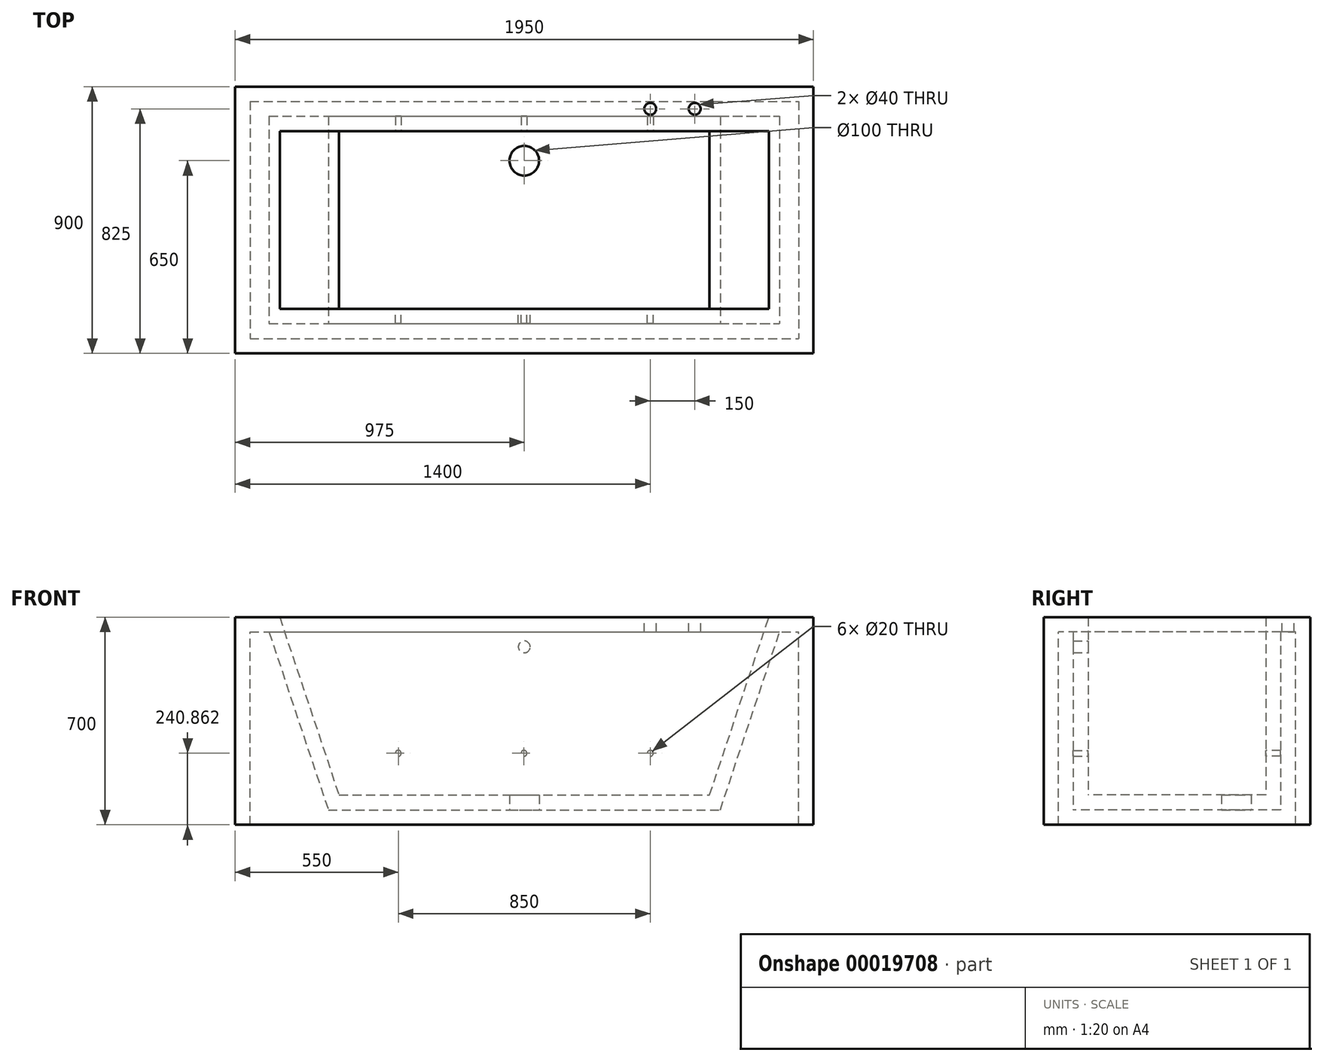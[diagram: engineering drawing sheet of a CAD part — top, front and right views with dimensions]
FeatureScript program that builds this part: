
annotation { "Feature Type Name" : "Feature", "Feature Type Description" : "" }
export const myFeature = defineFeature(function(context is Context, id is Id, definition is map)
    precondition{}
    {
        {
            var Q0;
            Q0=qCreatedBy(makeId("Front.planeOp"),FACE);
            var sketch = newSketch(context, id + "F0", { "sketchPlane" : qUnion([Q0])});
            skLineSegment(sketch, "E0.bottom", {"start": v(0, 0) * mm, "end": v(1950, 0) * mm});
            skLineSegment(sketch, "E0.top", {"start": v(0, 700) * mm, "end": v(1950, 700) * mm});
            skLineSegment(sketch, "E0.left", {"start": v(0, 0) * mm, "end": v(0, 700) * mm});
            skLineSegment(sketch, "E0.right", {"start": v(1950, 0) * mm, "end": v(1950, 700) * mm});
            skSolve(sketch);
        }
        {
            var Q0;
            Q0=makeQuery(id+"F0.imprint","IMPRINT",FACE,{"disambiguationData":[TD([[makeQuery(id+"F0.imprint","IMPRINT",EDGE,{"derivedFrom":sQuery(id+"F0.wireOp",EDGE,"E0.bottom")}),1.0]])]});
            var sketch = newSketch(context, id + "F1", { "sketchPlane" : qUnion([Q0])});
            skLineSegment(sketch, "E1", {"start": v(150, 700) * mm, "end": v(1800, 700) * mm});
            skLineSegment(sketch, "E2", {"start": v(150, 700) * mm, "end": v(350, 100) * mm});
            skLineSegment(sketch, "E3", {"start": v(350, 100) * mm, "end": v(1600, 100) * mm});
            skLineSegment(sketch, "E4", {"start": v(1600, 100) * mm, "end": v(1800, 700) * mm});
            skSolve(sketch);
        }
        {
            var Q0;
            Q0=makeQuery(id+"F0.imprint","IMPRINT",FACE,{"disambiguationData":[TD([[makeQuery(id+"F0.imprint","IMPRINT",EDGE,{"derivedFrom":sQuery(id+"F0.wireOp",EDGE,"E0.bottom")}),1.0]])]});
            extrude(context, id + "F2", {"entities" : qUnion([Q0]), "oppositeDirection" : true, "depth" : 450 * mm});
        }
        {
            var Q0;
            Q0=makeQuery(id+"F1.imprint","IMPRINT",FACE,{"disambiguationData":[TD([[makeQuery(id+"F1.imprint","IMPRINT",EDGE,{"derivedFrom":sQuery(id+"F1.wireOp",EDGE,"E1")}),-1.0]])]});
            extrude(context, id + "F3", {"entities" : qUnion([Q0]), "operationType" : NewBodyOperationType.REMOVE, "oppositeDirection" : true, "depth" : 300 * mm});
        }
        {
            var Q0;
            {var subQ0=makeQuery(id+"F2.opExtrude","SWEPT_FACE",FACE,{"disambiguationData":[OSD([sQuery(id+"F0.wireOp",EDGE,"E0.bottom")])]});Q0=makeQuery(id+"F7.boolean.opBoolean","MERGE",FACE,{"derivedFrom":[subQ0,makeQuery(id+"F7.opPattern","COPY",FACE,{"derivedFrom":subQ0,"instanceName":"1"})]});}
            var Q1;
            Q1=makeQuery(id+"F2.opExtrude","CAP_FACE",FACE,{"disambiguationData":[OSD([sQuery(id+"F0.wireOp",EDGE,"E0.bottom"),sQuery(id+"F0.wireOp",EDGE,"E0.top"),sQuery(id+"F0.wireOp",EDGE,"E0.left"),sQuery(id+"F0.wireOp",EDGE,"E0.right")])],"isStart":true});
            shell(context, id + "F4", {"entities" : qUnion([Q0, Q1]), "thickness" : 50 * mm});
        }
        {
            var Q0;
            Q0=makeQuery(id+"F3.boolean.opBoolean","COPY",FACE,{"derivedFrom":makeQuery(id+"F3.opExtrude","CAP_FACE",FACE,{"disambiguationData":[OSD([sQuery(id+"F1.wireOp",EDGE,"E1"),sQuery(id+"F1.wireOp",EDGE,"E2"),sQuery(id+"F1.wireOp",EDGE,"E3"),sQuery(id+"F1.wireOp",EDGE,"E4")])],"isStart":false})});
            var sketch = newSketch(context, id + "F5", { "sketchPlane" : qUnion([Q0])});
            skLineSegment(sketch, "E5", {"start": v(1600, 240.86) * mm, "end": v(1600, 100) * mm, "construction": true});
            skLineSegment(sketch, "E6", {"start": v(350, 240.86) * mm, "end": v(350, 100) * mm, "construction": true});
            skPoint(sketch, "E7", {"position": v(975, 240.86) * mm});
            skPoint(sketch, "E8", {"position": v(550, 240.86) * mm});
            skPoint(sketch, "E9", {"position": v(1400, 240.86) * mm});
            skLineSegment(sketch, "E10", {"start": v(350, 240.86) * mm, "end": v(550, 240.86) * mm, "construction": true});
            skLineSegment(sketch, "E11", {"start": v(1400, 240.86) * mm, "end": v(1600, 240.86) * mm, "construction": true});
            skLineSegment(sketch, "E12", {"start": v(550, 240.86) * mm, "end": v(1400, 240.86) * mm, "construction": true});
            skCircle(sketch, "E13", {"center": v(550, 240.86) * mm, "radius": 10 * mm});
            skCircle(sketch, "E14", {"center": v(974.1, 240.86) * mm, "radius": 10 * mm});
            skCircle(sketch, "E15", {"center": v(1400, 240.86) * mm, "radius": 10 * mm});
            skSolve(sketch);
        }
        {
            var Q0;
            Q0 = qSketchRegion(id + "F5", true);
            extrude(context, id + "F6", {"entities" : qUnion([Q0]), "operationType" : NewBodyOperationType.REMOVE, "oppositeDirection" : true, "depth" : 60 * mm});
        }
        {
            var Q0;
            Q0=makeQuery(id+"F2.opExtrude","SWEPT_BODY",BODY,{"disambiguationData":[OSD([sQuery(id+"F0.wireOp",EDGE,"E0.bottom"),sQuery(id+"F0.wireOp",EDGE,"E0.top"),sQuery(id+"F0.wireOp",EDGE,"E0.left"),sQuery(id+"F0.wireOp",EDGE,"E0.right")])]});
            var Q1;
            Q1=makeQuery(id+"F2.opExtrude","CAP_FACE",FACE,{"disambiguationData":[OSD([sQuery(id+"F0.wireOp",EDGE,"E0.bottom"),sQuery(id+"F0.wireOp",EDGE,"E0.top"),sQuery(id+"F0.wireOp",EDGE,"E0.left"),sQuery(id+"F0.wireOp",EDGE,"E0.right")])],"isStart":true});
            mirror(context, id + "F7", {"operationType" : NewBodyOperationType.ADD, "entities" : qUnion([Q0]), "mirrorPlane" : qUnion([Q1])});
        }
        {
            var Q0;
            {var subQ0=makeQuery(id+"F2.opExtrude","SWEPT_FACE",FACE,{"disambiguationData":[OSD([sQuery(id+"F0.wireOp",EDGE,"E0.top")])]});Q0=makeQuery(id+"F7.boolean.opBoolean","MERGE",FACE,{"derivedFrom":[subQ0,makeQuery(id+"F7.opPattern","COPY",FACE,{"derivedFrom":subQ0,"instanceName":"1"})]});}
            var sketch = newSketch(context, id + "F8", { "sketchPlane" : qUnion([Q0])});
            skLineSegment(sketch, "E16", {"start": v(1550, 450) * mm, "end": v(1550, 300) * mm, "construction": true});
            skLineSegment(sketch, "E17", {"start": v(1400, 450) * mm, "end": v(1400, 300) * mm, "construction": true});
            skLineSegment(sketch, "E18", {"start": v(0, 375) * mm, "end": v(1950, 375) * mm, "construction": true});
            skPoint(sketch, "E19", {"position": v(1400, 375) * mm});
            skPoint(sketch, "E20", {"position": v(1550, 375) * mm});
            skSolve(sketch);
        }
        {
            var Q0;
            Q0=sQuery(id+"F8.wireOp",VERTEX,"E20");
            var Q1;
            Q1=makeQuery(id+"F2.opExtrude","SWEPT_BODY",BODY,{"disambiguationData":[OSD([sQuery(id+"F0.wireOp",EDGE,"E0.bottom"),sQuery(id+"F0.wireOp",EDGE,"E0.top"),sQuery(id+"F0.wireOp",EDGE,"E0.left"),sQuery(id+"F0.wireOp",EDGE,"E0.right")])]});
            hole(context, id + "F9", {"style" : HoleStyle.SIMPLE, "holeDiameter" : 40 * mm, "endStyle" : HoleEndStyle.THROUGH, "locations" : qUnion([Q0]), "scope" : qUnion([Q1])});
        }
        {
            var Q0;
            Q0=sQuery(id+"F8.wireOp",VERTEX,"E19");
            var Q1;
            Q1=makeQuery(id+"F2.opExtrude","SWEPT_BODY",BODY,{"disambiguationData":[OSD([sQuery(id+"F0.wireOp",EDGE,"E0.bottom"),sQuery(id+"F0.wireOp",EDGE,"E0.top"),sQuery(id+"F0.wireOp",EDGE,"E0.left"),sQuery(id+"F0.wireOp",EDGE,"E0.right")])]});
            hole(context, id + "F10", {"style" : HoleStyle.SIMPLE, "holeDiameter" : 40 * mm, "endStyle" : HoleEndStyle.THROUGH, "locations" : qUnion([Q0]), "scope" : qUnion([Q1])});
        }
        {
            var Q0;
            Q0=makeQuery(id+"F4.opShell","OFFSET_FACE",FACE,{"disambiguationData":[OSD([sQuery(id+"F1.wireOp",EDGE,"E3")])]});
            var sketch = newSketch(context, id + "F11", { "sketchPlane" : qUnion([Q0])});
            skLineSegment(sketch, "E21", {"start": v(313.96, -200) * mm, "end": v(1636.04, -200) * mm, "construction": true});
            skPoint(sketch, "E22", {"position": v(975, -200) * mm});
            skSolve(sketch);
        }
        {
            var Q0;
            Q0=sQuery(id+"F11.wireOp",VERTEX,"E22");
            var Q1;
            Q1=makeQuery(id+"F2.opExtrude","SWEPT_BODY",BODY,{"disambiguationData":[OSD([sQuery(id+"F0.wireOp",EDGE,"E0.bottom"),sQuery(id+"F0.wireOp",EDGE,"E0.top"),sQuery(id+"F0.wireOp",EDGE,"E0.left"),sQuery(id+"F0.wireOp",EDGE,"E0.right")])]});
            hole(context, id + "F12", {"style" : HoleStyle.SIMPLE, "holeDiameter" : 100 * mm, "endStyle" : HoleEndStyle.THROUGH, "locations" : qUnion([Q0]), "scope" : qUnion([Q1])});
        }
        {
            var Q0;
            Q0=makeQuery(id+"F7.opPattern","COPY",FACE,{"derivedFrom":makeQuery(id+"F3.boolean.opBoolean","COPY",FACE,{"derivedFrom":makeQuery(id+"F3.opExtrude","CAP_FACE",FACE,{"disambiguationData":[OSD([sQuery(id+"F1.wireOp",EDGE,"E1"),sQuery(id+"F1.wireOp",EDGE,"E2"),sQuery(id+"F1.wireOp",EDGE,"E3"),sQuery(id+"F1.wireOp",EDGE,"E4")])],"isStart":false})}),"instanceName":"1"});
            var sketch = newSketch(context, id + "F13", { "sketchPlane" : qUnion([Q0])});
            skPoint(sketch, "E23", {"position": v(-975, 700) * mm});
            skLineSegment(sketch, "E24", {"start": v(-975, 700) * mm, "end": v(-975, 600) * mm, "construction": true});
            skSolve(sketch);
        }
        {
            var Q0;
            Q0=sQuery(id+"F13.wireOp",VERTEX,"E24.end");
            var Q1;
            Q1=makeQuery(id+"F2.opExtrude","SWEPT_BODY",BODY,{"disambiguationData":[OSD([sQuery(id+"F0.wireOp",EDGE,"E0.bottom"),sQuery(id+"F0.wireOp",EDGE,"E0.top"),sQuery(id+"F0.wireOp",EDGE,"E0.left"),sQuery(id+"F0.wireOp",EDGE,"E0.right")])]});
            hole(context, id + "F14", {"style" : HoleStyle.SIMPLE, "holeDiameter" : 40 * mm, "endStyle" : HoleEndStyle.BLIND, "holeDepth" : 60 * mm, "locations" : qUnion([Q0]), "scope" : qUnion([Q1])});
        }
    });
